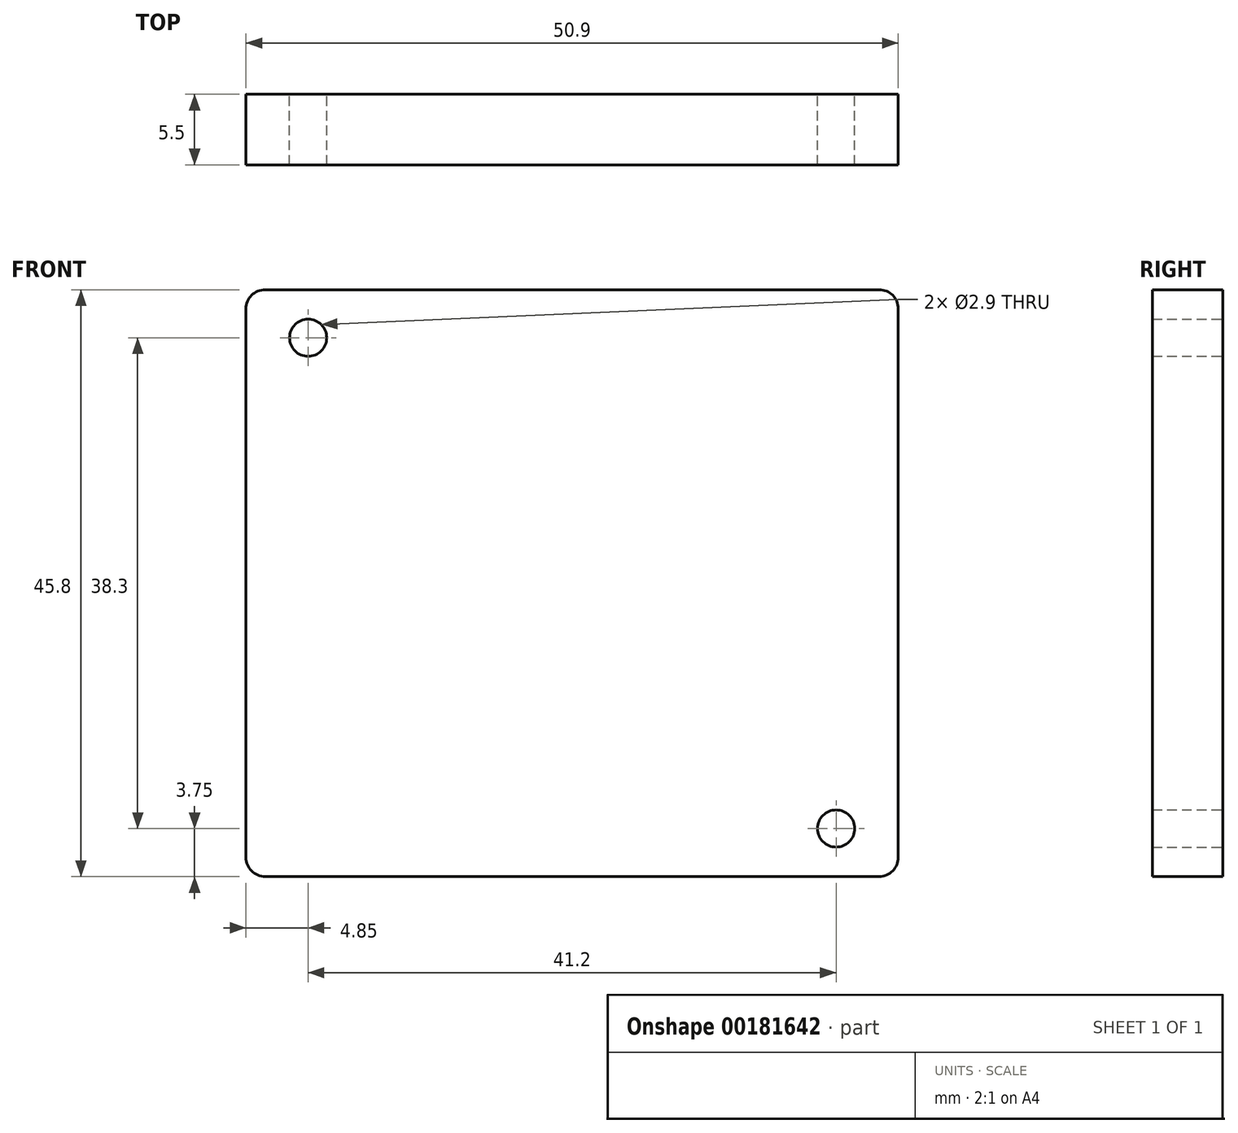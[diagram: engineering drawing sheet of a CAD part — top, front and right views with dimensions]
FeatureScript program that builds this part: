
annotation { "Feature Type Name" : "Feature", "Feature Type Description" : "" }
export const myFeature = defineFeature(function(context is Context, id is Id, definition is map)
    precondition{}
    {
        {
            var Q0;
            Q0=qCreatedBy(makeId("Front.planeOp"),FACE);
            var sketch = newSketch(context, id + "F0", { "sketchPlane" : qUnion([Q0])});
            skLineSegment(sketch, "E0.bottom", {"start": v(-23.95, 22.9) * mm, "end": v(23.95, 22.9) * mm});
            skLineSegment(sketch, "E0.top", {"start": v(-23.95, -22.9) * mm, "end": v(23.95, -22.9) * mm});
            skLineSegment(sketch, "E0.left", {"start": v(-25.45, 21.4) * mm, "end": v(-25.45, -21.4) * mm});
            skLineSegment(sketch, "E0.right", {"start": v(25.45, 21.4) * mm, "end": v(25.45, -21.4) * mm});
            skCircle(sketch, "E1", {"center": v(20.6, 19.15) * mm, "radius": 1.45 * mm});
            skCircle(sketch, "E2.MirrorC", {"center": v(-20.6, 19.15) * mm, "radius": 1.45 * mm});
            skCircle(sketch, "E3.MirrorC", {"center": v(-20.6, -19.15) * mm, "radius": 1.45 * mm});
            skCircle(sketch, "E4.MirrorC", {"center": v(20.6, -19.15) * mm, "radius": 1.45 * mm});
            skPoint(sketch, "E5.visualSharp", {"position": v(25.45, 22.9) * mm});
            skArc(sketch, "E5.filletArc", {"start": v(25.45, 21.4) * mm, "mid": v(25.01, 22.46) * mm, "end": v(23.95, 22.9) * mm});
            skArc(sketch, "E6.MirrorCS", {"start": v(-25.45, 21.4) * mm, "mid": v(-25.01, 22.46) * mm, "end": v(-23.95, 22.9) * mm});
            skArc(sketch, "E7.MirrorCS", {"start": v(-25.45, -21.4) * mm, "mid": v(-25.01, -22.46) * mm, "end": v(-23.95, -22.9) * mm});
            skArc(sketch, "E8.MirrorCS", {"start": v(25.45, -21.4) * mm, "mid": v(25.01, -22.46) * mm, "end": v(23.95, -22.9) * mm});
            skPoint(sketch, "E9.orphan", {"position": v(-25.45, 22.9) * mm});
            skPoint(sketch, "E10.orphan", {"position": v(25.45, -22.9) * mm});
            skSolve(sketch);
        }
        {
            var Q0;
            Q0=makeQuery(id+"F0.imprint","IMPRINT",FACE,{"disambiguationData":[TD([[makeQuery(id+"F0.imprint","IMPRINT",EDGE,{"derivedFrom":sQuery(id+"F0.wireOp",EDGE,"E0.bottom")}),-1.0]])]});
            var Q1;
            Q1=makeQuery(id+"F0.imprint","IMPRINT",FACE,{"disambiguationData":[TD([[makeQuery(id+"F0.imprint","IMPRINT",EDGE,{"derivedFrom":sQuery(id+"F0.wireOp",EDGE,"E1")}),1.0]])]});
            var Q2;
            Q2=makeQuery(id+"F0.imprint","IMPRINT",FACE,{"disambiguationData":[TD([[makeQuery(id+"F0.imprint","IMPRINT",EDGE,{"derivedFrom":sQuery(id+"F0.wireOp",EDGE,"E2.MirrorC")}),-1.0]])]});
            var Q3;
            Q3=makeQuery(id+"F0.imprint","IMPRINT",FACE,{"disambiguationData":[TD([[makeQuery(id+"F0.imprint","IMPRINT",EDGE,{"derivedFrom":sQuery(id+"F0.wireOp",EDGE,"E3.MirrorC")}),1.0]])]});
            var Q4;
            Q4=makeQuery(id+"F0.imprint","IMPRINT",FACE,{"disambiguationData":[TD([[makeQuery(id+"F0.imprint","IMPRINT",EDGE,{"derivedFrom":sQuery(id+"F0.wireOp",EDGE,"E4.MirrorC")}),-1.0]])]});
            extrude(context, id + "F1", {"entities" : qUnion([Q0, Q1, Q2, Q3, Q4]), "depth" : 4 * mm});
        }
        {
            var Q0;
            Q0=makeQuery(id+"F0.imprint","IMPRINT",FACE,{"disambiguationData":[TD([[makeQuery(id+"F0.imprint","IMPRINT",EDGE,{"derivedFrom":sQuery(id+"F0.wireOp",EDGE,"E3.MirrorC")}),1.0]])]});
            var Q1;
            Q1=makeQuery(id+"F0.imprint","IMPRINT",FACE,{"disambiguationData":[TD([[makeQuery(id+"F0.imprint","IMPRINT",EDGE,{"derivedFrom":sQuery(id+"F0.wireOp",EDGE,"E2.MirrorC")}),-1.0]])]});
            var Q2;
            Q2=makeQuery(id+"F0.imprint","IMPRINT",FACE,{"disambiguationData":[TD([[makeQuery(id+"F0.imprint","IMPRINT",EDGE,{"derivedFrom":sQuery(id+"F0.wireOp",EDGE,"E1")}),1.0]])]});
            var Q3;
            Q3=makeQuery(id+"F0.imprint","IMPRINT",FACE,{"disambiguationData":[TD([[makeQuery(id+"F0.imprint","IMPRINT",EDGE,{"derivedFrom":sQuery(id+"F0.wireOp",EDGE,"E4.MirrorC")}),-1.0]])]});
            extrude(context, id + "F2", {"entities" : qUnion([Q0, Q1, Q2, Q3]), "operationType" : NewBodyOperationType.ADD, "depth" : 5.5 * mm});
        }
    });
